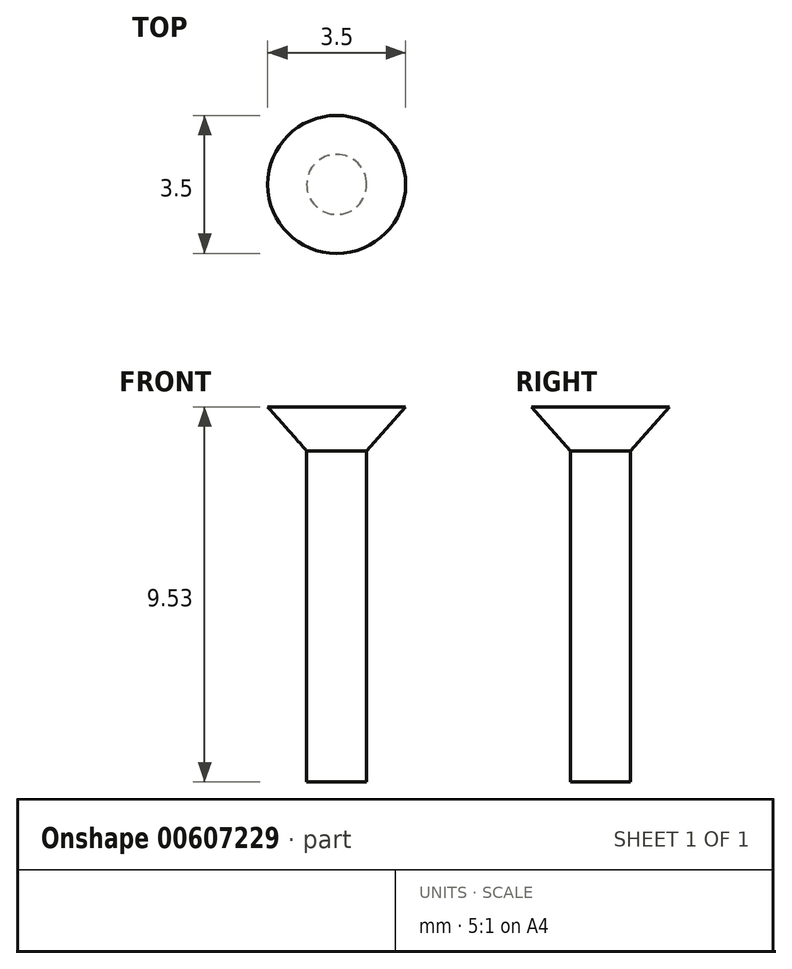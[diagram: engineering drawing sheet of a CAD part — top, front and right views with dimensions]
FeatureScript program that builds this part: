
annotation { "Feature Type Name" : "Feature", "Feature Type Description" : "" }
export const myFeature = defineFeature(function(context is Context, id is Id, definition is map)
    precondition{}
    {
        {
            var Q0;
            Q0=qCreatedBy(makeId("Front.planeOp"),FACE);
            var sketch = newSketch(context, id + "F0", { "sketchPlane" : qUnion([Q0])});
            skLineSegment(sketch, "E0", {"start": v(0, 0) * mm, "end": v(1.75, 0) * mm});
            skLineSegment(sketch, "E1", {"start": v(1.75, 0) * mm, "end": v(0.76, -1.12) * mm});
            skLineSegment(sketch, "E2", {"start": v(0.76, -1.12) * mm, "end": v(0.76, -9.53) * mm});
            skLineSegment(sketch, "E3", {"start": v(0.76, -9.53) * mm, "end": v(0, -9.53) * mm});
            skLineSegment(sketch, "E4", {"start": v(0, -9.53) * mm, "end": v(0, 0) * mm});
            skSolve(sketch);
        }
        {
            var Q0;
            Q0 = qSketchRegion(id + "F0", true);
            var Q1;
            Q1=sQuery(id+"F0.wireOp",EDGE,"E4");
            revolve(context, id + "F1", {"entities" : qUnion([Q0]), "axis" : qUnion([Q1]), "revolveType" : RevolveType.FULL});
        }
    });
